# Revit family: FP_Revit_18_CI704CTB1_Cooktop_90001894A
name_source: partatom
category: Specialty Equipment
revit_build: Autodesk Revit 2018 (Build: 20170223_1515(x64)
units: mm (PartAtom-declared; Revit-internal decimal feet)

## family parameters
Always vertical = Yes
Cut with Voids When Loaded = Yes
OmniClass Number = 23.40.40.14.17.11
OmniClass Title = Cookers, Ovens, Stoves
Part Type = Normal
Room Calculation Point = No
Round Connector Dimension = Use Diameter
Shared = No
Work Plane-Based = No

## types (1)
- FP_Revit_18_CI704CTB1_Cooktop_90001894A
    Cavity - Depth = 490 mm  [stored 1.60761 ft]
    Cavity - Height = 72 mm  [stored 0.23622 ft]
    Cavity - Width = 560 mm  [stored 1.83727 ft]
    Chassis - Depth = 485 mm  [stored 1.59121 ft]
    Chassis - Height = 56 mm  [stored 0.183727 ft]
    Chassis - Width = 555 mm  [stored 1.82087 ft]
    Clearance - Below = 72 mm  [stored 0.23622 ft]
    Clearance - Overhead Non-Combustible = 450 mm  [stored 1.47638 ft]
    Clearance - Overhead Rangehood = 650 mm  [stored 2.13255 ft]
    Clearance - Rear Combustible = 30 mm  [stored 0.0984252 ft]
    Clearance - Side Combustible = 30 mm  [stored 0.0984252 ft]
    Connector Note - Electrical = 220-240 V, 32 A, 50 Hz,
    Description = 70cm Induction Cooktop
    Manufacturer = Fisher & Paykel Appliances
    Material - Body = Fisher & Paykel - Grey
    Material - Glass = Fisher & Paykel - Glass, Black
    Material - Graphics = Fisher & Paykel - Graphics Grey
    Model = CI704CTB1
    Product - Depth = 530 mm  [stored 1.73885 ft]
    Product - Height = 61 mm  [stored 0.200131 ft]
    Product - Width = 700 mm  [stored 2.29659 ft]
    URL = www.fisherpaykel.com
    Visibility - Clearance Required = Yes

note: [stored X ft] marks values corroborated as IEEE doubles in the binary element streams (Revit-internal decimal feet)

## geometry (parser evidence)
native form markers: Sweep x4
no freeform markers — native parametric forms only
